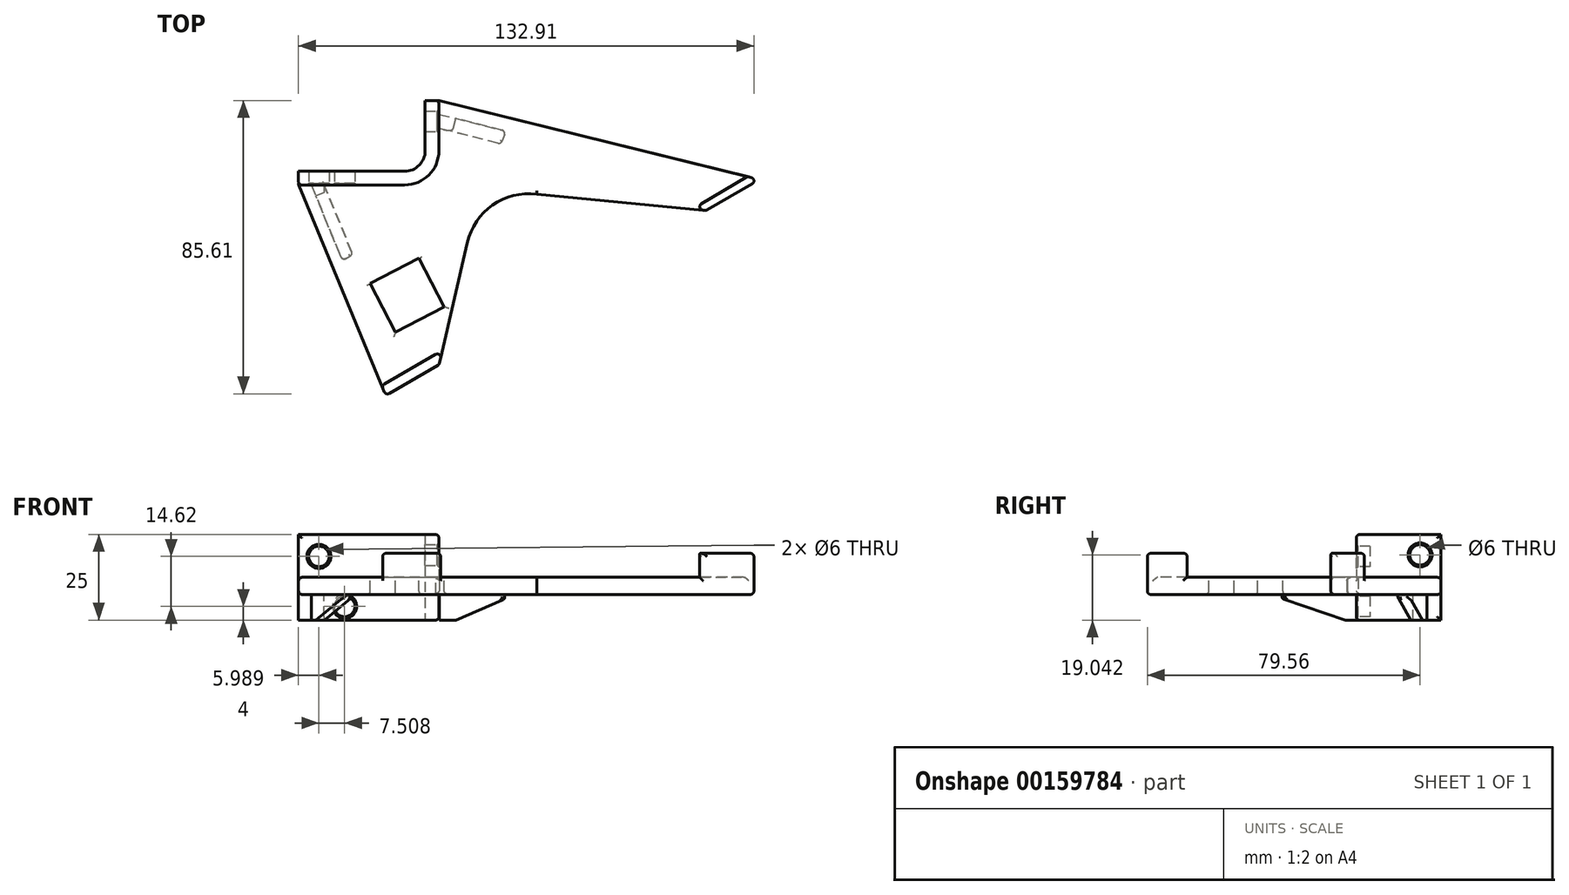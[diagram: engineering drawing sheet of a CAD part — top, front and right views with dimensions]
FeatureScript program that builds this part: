
annotation { "Feature Type Name" : "Feature", "Feature Type Description" : "" }
export const myFeature = defineFeature(function(context is Context, id is Id, definition is map)
    precondition{}
    {
        {
            var Q0;
            Q0=qCreatedBy(makeId("Top.planeOp"),FACE);
            var sketch = newSketch(context, id + "F0", { "sketchPlane" : qUnion([Q0])});
            skLineSegment(sketch, "E0", {"start": v(0, 24.64) * mm, "end": v(0, 10) * mm});
            skLineSegment(sketch, "E1", {"start": v(-41, 0) * mm, "end": v(-10, 0) * mm});
            skPoint(sketch, "E2.visualSharp", {"position": v(0, 0) * mm});
            skArc(sketch, "E2.filletArc", {"start": v(-10, 0) * mm, "mid": v(-2.93, 2.93) * mm, "end": v(0, 10) * mm});
            skLineSegment(sketch, "E3.0", {"start": v(-4, 24.64) * mm, "end": v(-4, 10) * mm});
            skArc(sketch, "E3.1", {"start": v(-10, 4) * mm, "mid": v(-5.76, 5.76) * mm, "end": v(-4, 10) * mm});
            skLineSegment(sketch, "E3.2", {"start": v(-41, 4) * mm, "end": v(-10, 4) * mm});
            skLineSegment(sketch, "E4", {"start": v(-4, 24.64) * mm, "end": v(-4, 24.64) * mm});
            skPoint(sketch, "E5.end.orphan", {"position": v(0, 30.23) * mm});
            skPoint(sketch, "E6.orphan", {"position": v(-2.7, 27.44) * mm});
            skPoint(sketch, "E7.start.orphan", {"position": v(0, 27.44) * mm});
            skLineSegment(sketch, "E8", {"start": v(0, 24.64) * mm, "end": v(-4, 24.64) * mm});
            skLineSegment(sketch, "E9", {"start": v(-41, 4) * mm, "end": v(-41, 0) * mm});
            skLineSegment(sketch, "E10", {"start": v(0, 0) * mm, "end": v(-66, 0) * mm});
            skLineSegment(sketch, "E11", {"start": v(-66, 0) * mm, "end": v(-66, -100) * mm});
            skLineSegment(sketch, "E12", {"start": v(-66, 0) * mm, "end": v(-66, 0) * mm});
            skLineSegment(sketch, "E13", {"start": v(0, 0) * mm, "end": v(-41, 0) * mm});
            skLineSegment(sketch, "E14", {"start": v(-25.5, 0) * mm, "end": v(-41, 0) * mm});
            skLineSegment(sketch, "E15.bottom", {"start": v(-22.01, -78.96) * mm, "end": v(134.2, 11.23) * mm});
            skLineSegment(sketch, "E15.top", {"start": v(0.49, -117.93) * mm, "end": v(156.7, -27.74) * mm});
            skLineSegment(sketch, "E15.left", {"start": v(-22.01, -78.96) * mm, "end": v(0.49, -117.93) * mm});
            skLineSegment(sketch, "E16", {"start": v(0, 24.64) * mm, "end": v(93.48, 1.57) * mm});
            skLineSegment(sketch, "E17", {"start": v(-41, 0) * mm, "end": v(-15.59, -61.4) * mm});
            skLineSegment(sketch, "E18", {"start": v(-15.59, -61.4) * mm, "end": v(0, -52.4) * mm});
            skLineSegment(sketch, "E19", {"start": v(93.48, 1.57) * mm, "end": v(77.9, -7.43) * mm});
            skLineSegment(sketch, "E20", {"start": v(77.9, -7.43) * mm, "end": v(28.44, -2.71) * mm});
            skLineSegment(sketch, "E21", {"start": v(0, -52.4) * mm, "end": v(8.17, -16.87) * mm});
            skArc(sketch, "E22", {"start": v(28.44, -2.71) * mm, "mid": v(15.58, -5.89) * mm, "end": v(8.17, -16.87) * mm});
            skLineSegment(sketch, "E23", {"start": v(13.32, -41.68) * mm, "end": v(-9.18, -2.7) * mm});
            skSolve(sketch);
        }
        {
            var Q0;
            Q0=qSketchRegion(id+"F0",true);
            extrude(context, id + "F1", {"entities" : qUnion([Q0]), "endBound" : BoundingType.SYMMETRIC, "depth" : 5 * mm});
        }
        {
            var Q0;
            Q0=qCreatedBy(makeId("Top.planeOp"),FACE);
            var sketch = newSketch(context, id + "F2", { "sketchPlane" : qUnion([Q0])});
            skLineSegment(sketch, "E24", {"start": v(-0.08, 24.65) * mm, "end": v(-0.08, 10.01) * mm});
            skArc(sketch, "E25.filletArc", {"start": v(-10.08, 0.01) * mm, "mid": v(-3, 2.94) * mm, "end": v(-0.08, 10.01) * mm});
            skLineSegment(sketch, "E26.0", {"start": v(-4.08, 24.65) * mm, "end": v(-4.08, 10.01) * mm});
            skArc(sketch, "E26.1", {"start": v(-10.08, 4.01) * mm, "mid": v(-5.84, 5.77) * mm, "end": v(-4.08, 10.01) * mm});
            skLineSegment(sketch, "E26.2", {"start": v(-41.08, 4.01) * mm, "end": v(-10.08, 4.01) * mm});
            skLineSegment(sketch, "E27", {"start": v(-9.33, 43.65) * mm, "end": v(-9.33, 43.65) * mm});
            skLineSegment(sketch, "E28", {"start": v(-0.08, 24.65) * mm, "end": v(-4.08, 24.65) * mm});
            skLineSegment(sketch, "E29", {"start": v(-41.08, 4.01) * mm, "end": v(-41.08, 0.01) * mm});
            skLineSegment(sketch, "E30", {"start": v(-10.08, 0.01) * mm, "end": v(-41.08, 0.01) * mm});
            skSolve(sketch);
        }
        {
            var Q0;
            Q0=qSketchRegion(id+"F2",true);
            extrude(context, id + "F3", {"entities" : qUnion([Q0]), "operationType" : NewBodyOperationType.ADD, "depth" : 15 * mm, "hasSecondDirection" : true, "secondDirectionOppositeDirection" : true, "secondDirectionDepth" : 10 * mm});
        }
        {
            var Q0;
            Q0=qCreatedBy(makeId("Top.planeOp"),FACE);
            var sketch = newSketch(context, id + "F4", { "sketchPlane" : qUnion([Q0])});
            skLineSegment(sketch, "E31", {"start": v(-40.71, 0) * mm, "end": v(-31.48, -22.47) * mm});
            skLineSegment(sketch, "E32", {"start": v(-37.87, 1.4) * mm, "end": v(-28.24, -22.05) * mm});
            skLineSegment(sketch, "E33", {"start": v(-28.24, -22.05) * mm, "end": v(-25.23, -20.31) * mm});
            skLineSegment(sketch, "E34", {"start": v(-25.23, -20.31) * mm, "end": v(-34.15, 1.4) * mm});
            skLineSegment(sketch, "E35", {"start": v(-34.15, 1.4) * mm, "end": v(-37.87, 1.4) * mm});
            skSolve(sketch);
        }
        {
            var Q0;
            Q0 = qSketchRegion(id + "F4", true);
            extrude(context, id + "F5", {"entities" : qUnion([Q0]), "operationType" : NewBodyOperationType.ADD, "oppositeDirection" : true, "depth" : 10 * mm});
        }
        {
            var Q0;
            Q0=qCreatedBy(makeId("Top.planeOp"),FACE);
            var sketch = newSketch(context, id + "F6", { "sketchPlane" : qUnion([Q0])});
            skLineSegment(sketch, "E36", {"start": v(-41.47, 0) * mm, "end": v(-37.36, 0) * mm});
            skLineSegment(sketch, "E37", {"start": v(0, 20.6) * mm, "end": v(19.4, 15.74) * mm});
            skLineSegment(sketch, "E38", {"start": v(19.4, 15.74) * mm, "end": v(18.07, 11.97) * mm});
            skLineSegment(sketch, "E39", {"start": v(18.07, 11.97) * mm, "end": v(0, 16.49) * mm});
            skLineSegment(sketch, "E40", {"start": v(0, 16.49) * mm, "end": v(0, 20.6) * mm});
            skLineSegment(sketch, "E41", {"start": v(0, 18.54) * mm, "end": v(0, 20.6) * mm});
            skSolve(sketch);
        }
        {
            var Q0;
            Q0 = qSketchRegion(id + "F6", true);
            extrude(context, id + "F7", {"entities" : qUnion([Q0]), "operationType" : NewBodyOperationType.ADD, "oppositeDirection" : true, "depth" : 10 * mm});
        }
        {
            var Q0;
            Q0=qCreatedBy(makeId("Top.planeOp"),FACE);
            var sketch = newSketch(context, id + "F8", { "sketchPlane" : qUnion([Q0])});
            skLineSegment(sketch, "E42.bottom", {"start": v(-20.1, -28.78) * mm, "end": v(-5.9, -21.4) * mm});
            skLineSegment(sketch, "E42.top", {"start": v(-12.73, -42.97) * mm, "end": v(1.47, -35.6) * mm});
            skLineSegment(sketch, "E42.left", {"start": v(-20.1, -28.78) * mm, "end": v(-12.73, -42.97) * mm});
            skLineSegment(sketch, "E42.right", {"start": v(-5.9, -21.4) * mm, "end": v(1.47, -35.6) * mm});
            skSolve(sketch);
        }
        {
            var Q0;
            Q0 = qSketchRegion(id + "F8", true);
            extrude(context, id + "F9", {"entities" : qUnion([Q0]), "operationType" : NewBodyOperationType.REMOVE, "endBound" : BoundingType.SYMMETRIC, "oppositeDirection" : true, "depth" : 25 * mm});
        }
        {
            var Q0;
            Q0=makeQuery(id+"F5.opExtrude","SWEPT_FACE",FACE,{"disambiguationData":[OSD([sQuery(id+"F4.wireOp",EDGE,"E32")])]});
            var sketch = newSketch(context, id + "F10", { "sketchPlane" : qUnion([Q0])});
            skLineSegment(sketch, "E43", {"start": v(9.66, -3.57) * mm, "end": v(-10.72, -10) * mm});
            skLineSegment(sketch, "E44", {"start": v(-10.72, -10) * mm, "end": v(9.66, -10) * mm});
            skLineSegment(sketch, "E45", {"start": v(9.66, -10) * mm, "end": v(9.66, -3.57) * mm});
            skSolve(sketch);
        }
        {
            var Q0;
            Q0=makeQuery(id+"F10.imprint","IMPRINT",FACE,{"disambiguationData":[TD([[makeQuery(id+"F10.imprint","IMPRINT",EDGE,{"derivedFrom":sQuery(id+"F10.wireOp",EDGE,"E43")}),1.0]])]});
            extrude(context, id + "F11", {"entities" : qUnion([Q0]), "operationType" : NewBodyOperationType.REMOVE, "oppositeDirection" : true, "depth" : 7 * mm});
        }
        {
            var Q0;
            Q0=makeQuery(id+"F7.opExtrude","SWEPT_FACE",FACE,{"disambiguationData":[OSD([sQuery(id+"F6.wireOp",EDGE,"E37")])]});
            var sketch = newSketch(context, id + "F12", { "sketchPlane" : qUnion([Q0])});
            skLineSegment(sketch, "E46", {"start": v(-15, -3.7) * mm, "end": v(0, -10) * mm});
            skLineSegment(sketch, "E47", {"start": v(0, -10) * mm, "end": v(-15, -10) * mm});
            skLineSegment(sketch, "E48", {"start": v(-15, -10) * mm, "end": v(-15, -3.7) * mm});
            skSolve(sketch);
        }
        {
            var Q0;
            Q0=makeQuery(id+"F12.imprint","IMPRINT",FACE,{"disambiguationData":[TD([[makeQuery(id+"F12.imprint","IMPRINT",EDGE,{"derivedFrom":sQuery(id+"F12.wireOp",EDGE,"E46")}),-1.0]])]});
            extrude(context, id + "F13", {"entities" : qUnion([Q0]), "operationType" : NewBodyOperationType.REMOVE, "oppositeDirection" : true, "depth" : 7 * mm});
        }
        {
            var Q0;
            Q0=makeQuery(id+"F1.opExtrude","CAP_FACE",FACE,{"disambiguationData":[OSD([sQuery(id+"F0.wireOp",EDGE,"E3.0"),sQuery(id+"F0.wireOp",EDGE,"E3.1"),sQuery(id+"F0.wireOp",EDGE,"E3.2"),sQuery(id+"F0.wireOp",EDGE,"E8"),sQuery(id+"F0.wireOp",EDGE,"E9"),sQuery(id+"F0.wireOp",EDGE,"E16"),sQuery(id+"F0.wireOp",EDGE,"E17"),sQuery(id+"F0.wireOp",EDGE,"E18"),sQuery(id+"F0.wireOp",EDGE,"E19"),sQuery(id+"F0.wireOp",EDGE,"E20"),sQuery(id+"F0.wireOp",EDGE,"E21"),sQuery(id+"F0.wireOp",EDGE,"E22")])],"isStart":false});
            var sketch = newSketch(context, id + "F14", { "sketchPlane" : qUnion([Q0])});
            skLineSegment(sketch, "E49", {"start": v(-15.59, -61.4) * mm, "end": v(0, -52.4) * mm});
            skLineSegment(sketch, "E50", {"start": v(0, -52.4) * mm, "end": v(0.94, -48.3) * mm});
            skLineSegment(sketch, "E51", {"start": v(0.94, -48.3) * mm, "end": v(-16.77, -58.54) * mm});
            skLineSegment(sketch, "E52", {"start": v(-16.77, -58.54) * mm, "end": v(-15.59, -61.4) * mm});
            skSolve(sketch);
        }
        {
            var Q0;
            Q0=makeQuery(id+"F14.imprint","IMPRINT",FACE,{"disambiguationData":[TD([[makeQuery(id+"F14.imprint","IMPRINT",EDGE,{"derivedFrom":sQuery(id+"F14.wireOp",EDGE,"E49")}),1.0]])]});
            extrude(context, id + "F15", {"entities" : qUnion([Q0]), "operationType" : NewBodyOperationType.ADD, "depth" : 7 * mm});
        }
        {
            var Q0;
            Q0=makeQuery(id+"F1.opExtrude","CAP_FACE",FACE,{"disambiguationData":[OSD([sQuery(id+"F0.wireOp",EDGE,"E3.0"),sQuery(id+"F0.wireOp",EDGE,"E3.1"),sQuery(id+"F0.wireOp",EDGE,"E3.2"),sQuery(id+"F0.wireOp",EDGE,"E8"),sQuery(id+"F0.wireOp",EDGE,"E9"),sQuery(id+"F0.wireOp",EDGE,"E16"),sQuery(id+"F0.wireOp",EDGE,"E17"),sQuery(id+"F0.wireOp",EDGE,"E18"),sQuery(id+"F0.wireOp",EDGE,"E19"),sQuery(id+"F0.wireOp",EDGE,"E20"),sQuery(id+"F0.wireOp",EDGE,"E21"),sQuery(id+"F0.wireOp",EDGE,"E22")])],"isStart":false});
            var sketch = newSketch(context, id + "F16", { "sketchPlane" : qUnion([Q0])});
            skLineSegment(sketch, "E53", {"start": v(77.9, -7.43) * mm, "end": v(93.48, 1.57) * mm});
            skLineSegment(sketch, "E54", {"start": v(93.48, 1.57) * mm, "end": v(89.9, 2.46) * mm});
            skLineSegment(sketch, "E55", {"start": v(89.9, 2.46) * mm, "end": v(73.9, -7.05) * mm});
            skLineSegment(sketch, "E56", {"start": v(73.9, -7.05) * mm, "end": v(77.9, -7.43) * mm});
            skSolve(sketch);
        }
        {
            var Q0;
            Q0=makeQuery(id+"F16.imprint","IMPRINT",FACE,{"disambiguationData":[TD([[makeQuery(id+"F16.imprint","IMPRINT",EDGE,{"derivedFrom":sQuery(id+"F16.wireOp",EDGE,"E53")}),-1.0]])]});
            extrude(context, id + "F17", {"entities" : qUnion([Q0]), "operationType" : NewBodyOperationType.ADD, "depth" : 7 * mm});
        }
        {
            var Q0;
            Q0=makeQuery(id+"FxJEatKh2n8C777_1.opFillet","SPLIT",FACE,{"disambiguationData":[OD(1.0)],"derivedFrom":makeQuery(id+"F3.opExtrude","SWEPT_FACE",FACE,{"disambiguationData":[OSD([sQuery(id+"F2.wireOp",EDGE,"E30")])]})});
            var sketch = newSketch(context, id + "F18", { "sketchPlane" : qUnion([Q0])});
            skLineSegment(sketch, "E57.bottom", {"start": v(-41.1, 14.62) * mm, "end": v(-35.1, 14.62) * mm});
            skLineSegment(sketch, "E57.top", {"start": v(-41.1, 8.62) * mm, "end": v(-35.1, 8.62) * mm});
            skLineSegment(sketch, "E57.left", {"start": v(-41.1, 14.62) * mm, "end": v(-41.1, 8.62) * mm});
            skLineSegment(sketch, "E57.right", {"start": v(-35.1, 14.62) * mm, "end": v(-35.1, 8.62) * mm});
            skPoint(sketch, "E58", {"position": v(-35.1, 8.62) * mm});
            skSolve(sketch);
        }
        {
            var Q0;
            {var subQ1=sQuery(id+"F4.wireOp",EDGE,"E34");var subQ2=sQuery(id+"F2.wireOp",EDGE,"E30");Q0=makeQuery(id+"F5.boolean.opBoolean","SPLIT",FACE,{"disambiguationData":[TD([makeQuery(id+"F5.opExtrude","SWEPT_FACE",FACE,{"disambiguationData":[OSD([subQ1])]})])],"derivedFrom":makeQuery(id+"F3.opExtrude","SWEPT_FACE",FACE,{"disambiguationData":[OSD([subQ2])]})});}
            var sketch = newSketch(context, id + "F19", { "sketchPlane" : qUnion([Q0])});
            skLineSegment(sketch, "E59.bottom", {"start": v(-33.58, -10) * mm, "end": v(-27.58, -10) * mm});
            skLineSegment(sketch, "E59.top", {"start": v(-33.58, -6) * mm, "end": v(-27.58, -6) * mm});
            skLineSegment(sketch, "E59.left", {"start": v(-33.58, -10) * mm, "end": v(-33.58, -6) * mm});
            skLineSegment(sketch, "E59.right", {"start": v(-27.58, -10) * mm, "end": v(-27.58, -6) * mm});
            skPoint(sketch, "E60", {"position": v(-27.58, -6) * mm});
            skSolve(sketch);
        }
        {
            var Q0;
            Q0=makeQuery(id+"F3.opExtrude","SWEPT_FACE",FACE,{"disambiguationData":[OSD([sQuery(id+"F2.wireOp",EDGE,"E24")])]});
            var sketch = newSketch(context, id + "F20", { "sketchPlane" : qUnion([Q0])});
            skLineSegment(sketch, "E61.bottom", {"start": v(24.6, 15.04) * mm, "end": v(18.6, 15.04) * mm});
            skLineSegment(sketch, "E61.top", {"start": v(24.6, 9.04) * mm, "end": v(18.6, 9.04) * mm});
            skLineSegment(sketch, "E61.left", {"start": v(24.6, 15.04) * mm, "end": v(24.6, 9.04) * mm});
            skLineSegment(sketch, "E61.right", {"start": v(18.6, 15.04) * mm, "end": v(18.6, 9.04) * mm});
            skPoint(sketch, "E62", {"position": v(18.6, 9.04) * mm});
            skSolve(sketch);
        }
        {
            var Q0;
            Q0=sQuery(id+"F18.wireOp",VERTEX,"E58");
            var Q1;
            Q1=sQuery(id+"F20.wireOp",VERTEX,"E62");
            var Q2;
            Q2=sQuery(id+"F19.wireOp",VERTEX,"E60");
            var Q3;
            Q3=makeQuery(id+"F1.opExtrude","SWEPT_BODY",BODY,{"disambiguationData":[OSD([sQuery(id+"F0.wireOp",EDGE,"E3.0"),sQuery(id+"F0.wireOp",EDGE,"E3.1"),sQuery(id+"F0.wireOp",EDGE,"E3.2"),sQuery(id+"F0.wireOp",EDGE,"E8"),sQuery(id+"F0.wireOp",EDGE,"E9"),sQuery(id+"F0.wireOp",EDGE,"E16"),sQuery(id+"F0.wireOp",EDGE,"E17"),sQuery(id+"F0.wireOp",EDGE,"E18"),sQuery(id+"F0.wireOp",EDGE,"E19"),sQuery(id+"F0.wireOp",EDGE,"E20"),sQuery(id+"F0.wireOp",EDGE,"E21"),sQuery(id+"F0.wireOp",EDGE,"E22")])]});
            hole(context, id + "F21", {"style" : HoleStyle.C_SINK, "endStyle" : HoleEndStyle.THROUGH, "holeDiameter" : 6 * mm, "cSinkDiameter" : 7 * mm, "cSinkAngle" : 90 * degree, "locations" : qUnion([Q0, Q1, Q2]), "scope" : qUnion([Q3]), "isTappedThrough" : true});
        }
        {
            var Q0;
            Q0=makeQuery(id+"F15.boolean.opBoolean","MERGE",EDGE,{"derivedFrom":[makeQuery(id+"F1.opExtrude","SWEPT_EDGE",EDGE,{"disambiguationData":[OSD([sQuery(id+"F0.wireOp",EDGE,"E17"),sQuery(id+"F0.wireOp",EDGE,"E18")])]}),makeQuery(id+"F15.opExtrude","SWEPT_EDGE",EDGE,{"disambiguationData":[OSD([sQuery(id+"F14.wireOp",EDGE,"E49"),sQuery(id+"F14.wireOp",EDGE,"E52")])]})]});
            var Q1;
            Q1=makeQuery(id+"F15.boolean.opBoolean","MERGE",FACE,{"derivedFrom":[makeQuery(id+"F1.opExtrude","SWEPT_FACE",FACE,{"disambiguationData":[OSD([sQuery(id+"F0.wireOp",EDGE,"E18")])]}),makeQuery(id+"F15.opExtrude","SWEPT_FACE",FACE,{"disambiguationData":[OSD([sQuery(id+"F14.wireOp",EDGE,"E49")])]})]});
            var Q2;
            Q2=makeQuery(id+"F1.opExtrude","CAP_EDGE",EDGE,{"disambiguationData":[OSD([sQuery(id+"F0.wireOp",EDGE,"E17")])],"isStart":false});
            var Q3;
            Q3=makeQuery(id+"F15.boolean.opBoolean","MERGE",FACE,{"derivedFrom":[makeQuery(id+"F1.opExtrude","SWEPT_FACE",FACE,{"disambiguationData":[OSD([sQuery(id+"F0.wireOp",EDGE,"E17")])]}),makeQuery(id+"F15.opExtrude","SWEPT_FACE",FACE,{"disambiguationData":[OSD([sQuery(id+"F14.wireOp",EDGE,"E52")])]})]});
            var Q4;
            Q4=makeQuery(id+"F15.boolean.opBoolean","MERGE",FACE,{"derivedFrom":[makeQuery(id+"F1.opExtrude","SWEPT_FACE",FACE,{"disambiguationData":[OSD([sQuery(id+"F0.wireOp",EDGE,"E21")])]}),makeQuery(id+"F15.opExtrude","SWEPT_FACE",FACE,{"disambiguationData":[OSD([sQuery(id+"F14.wireOp",EDGE,"E50")])]})]});
            var Q5;
            Q5=makeQuery(id+"F1.opExtrude","CAP_EDGE",EDGE,{"disambiguationData":[OSD([sQuery(id+"F0.wireOp",EDGE,"E20")])],"isStart":false});
            var Q6;
            Q6=makeQuery(id+"F1.opExtrude","CAP_EDGE",EDGE,{"disambiguationData":[OSD([sQuery(id+"F0.wireOp",EDGE,"E20")])],"isStart":true});
            var Q7;
            Q7=makeQuery(id+"F11.boolean.opBoolean","INTERSECT",EDGE,{"derivedFrom":[makeQuery(id+"F5.opExtrude","SWEPT_FACE",FACE,{"disambiguationData":[OSD([sQuery(id+"F4.wireOp",EDGE,"E33")])]}),makeQuery(id+"F11.opExtrude","SWEPT_FACE",FACE,{"disambiguationData":[OSD([sQuery(id+"F10.wireOp",EDGE,"E43")])]})]});
            var Q8;
            Q8=makeQuery(id+"F11.boolean.opBoolean","COPY",EDGE,{"derivedFrom":makeQuery(id+"F11.opExtrude","CAP_EDGE",EDGE,{"disambiguationData":[OSD([sQuery(id+"F10.wireOp",EDGE,"E43")])],"isStart":true})});
            var Q9;
            Q9=makeQuery(id+"F5.opExtrude","SWEPT_EDGE",EDGE,{"disambiguationData":[OSD([sQuery(id+"F4.wireOp",EDGE,"E33"),sQuery(id+"F4.wireOp",EDGE,"E34")])]});
            var Q10;
            Q10=makeQuery(id+"F11.boolean.opBoolean","INTERSECT",EDGE,{"derivedFrom":[makeQuery(id+"F5.opExtrude","SWEPT_FACE",FACE,{"disambiguationData":[OSD([sQuery(id+"F4.wireOp",EDGE,"E34")])]}),makeQuery(id+"F11.opExtrude","SWEPT_FACE",FACE,{"disambiguationData":[OSD([sQuery(id+"F10.wireOp",EDGE,"E43")])]})]});
            var Q11;
            Q11=makeQuery(id+"F5.opExtrude","SWEPT_EDGE",EDGE,{"disambiguationData":[OSD([sQuery(id+"F4.wireOp",EDGE,"E32"),sQuery(id+"F4.wireOp",EDGE,"E33")])]});
            var Q12;
            Q12=makeQuery(id+"F13.boolean.opBoolean","INTERSECT",EDGE,{"derivedFrom":[makeQuery(id+"F7.opExtrude","SWEPT_FACE",FACE,{"disambiguationData":[OSD([sQuery(id+"F6.wireOp",EDGE,"E39")])]}),makeQuery(id+"F13.opExtrude","SWEPT_FACE",FACE,{"disambiguationData":[OSD([sQuery(id+"F12.wireOp",EDGE,"E46")])]})]});
            var Q13;
            Q13=makeQuery(id+"F7.opExtrude","SWEPT_EDGE",EDGE,{"disambiguationData":[OSD([sQuery(id+"F6.wireOp",EDGE,"E38"),sQuery(id+"F6.wireOp",EDGE,"E39")])]});
            var Q14;
            Q14=makeQuery(id+"F7.opExtrude","SWEPT_EDGE",EDGE,{"disambiguationData":[OSD([sQuery(id+"F6.wireOp",EDGE,"E37"),sQuery(id+"F6.wireOp",EDGE,"E38")])]});
            var Q15;
            Q15=makeQuery(id+"F1.opExtrude","CAP_EDGE",EDGE,{"disambiguationData":[OSD([sQuery(id+"F0.wireOp",EDGE,"E16")])],"isStart":false});
            var Q16;
            Q16=makeQuery(id+"F17.opExtrude","SWEPT_EDGE",EDGE,{"disambiguationData":[OSD([sQuery(id+"F0.wireOp",EDGE,"E16"),sQuery(id+"F16.wireOp",EDGE,"E54"),sQuery(id+"F16.wireOp",EDGE,"E55")])]});
            var Q17;
            Q17=makeQuery(id+"F13.boolean.opBoolean","INTERSECT",EDGE,{"derivedFrom":[makeQuery(id+"F7.opExtrude","SWEPT_FACE",FACE,{"disambiguationData":[OSD([sQuery(id+"F6.wireOp",EDGE,"E38")])]}),makeQuery(id+"F13.opExtrude","SWEPT_FACE",FACE,{"disambiguationData":[OSD([sQuery(id+"F12.wireOp",EDGE,"E46")])]})]});
            var Q18;
            Q18=makeQuery(id+"F13.boolean.opBoolean","COPY",EDGE,{"derivedFrom":makeQuery(id+"F13.opExtrude","CAP_EDGE",EDGE,{"disambiguationData":[OSD([sQuery(id+"F12.wireOp",EDGE,"E46")])],"isStart":true})});
            var Q19;
            Q19=makeQuery(id+"F9.boolean.opBoolean","INTERSECT",EDGE,{"derivedFrom":[makeQuery(id+"F1.opExtrude","CAP_FACE",FACE,{"disambiguationData":[OSD([sQuery(id+"F0.wireOp",EDGE,"E3.0"),sQuery(id+"F0.wireOp",EDGE,"E3.1"),sQuery(id+"F0.wireOp",EDGE,"E3.2"),sQuery(id+"F0.wireOp",EDGE,"E8"),sQuery(id+"F0.wireOp",EDGE,"E9"),sQuery(id+"F0.wireOp",EDGE,"E16"),sQuery(id+"F0.wireOp",EDGE,"E17"),sQuery(id+"F0.wireOp",EDGE,"E18"),sQuery(id+"F0.wireOp",EDGE,"E19"),sQuery(id+"F0.wireOp",EDGE,"E20"),sQuery(id+"F0.wireOp",EDGE,"E21"),sQuery(id+"F0.wireOp",EDGE,"E22")])],"isStart":true}),makeQuery(id+"F9.opExtrude","SWEPT_FACE",FACE,{"disambiguationData":[OSD([sQuery(id+"F8.wireOp",EDGE,"E42.left")])]})]});
            var Q20;
            Q20=makeQuery(id+"F9.boolean.opBoolean","INTERSECT",EDGE,{"derivedFrom":[makeQuery(id+"F1.opExtrude","CAP_FACE",FACE,{"disambiguationData":[OSD([sQuery(id+"F0.wireOp",EDGE,"E3.0"),sQuery(id+"F0.wireOp",EDGE,"E3.1"),sQuery(id+"F0.wireOp",EDGE,"E3.2"),sQuery(id+"F0.wireOp",EDGE,"E8"),sQuery(id+"F0.wireOp",EDGE,"E9"),sQuery(id+"F0.wireOp",EDGE,"E16"),sQuery(id+"F0.wireOp",EDGE,"E17"),sQuery(id+"F0.wireOp",EDGE,"E18"),sQuery(id+"F0.wireOp",EDGE,"E19"),sQuery(id+"F0.wireOp",EDGE,"E20"),sQuery(id+"F0.wireOp",EDGE,"E21"),sQuery(id+"F0.wireOp",EDGE,"E22")])],"isStart":true}),makeQuery(id+"F9.opExtrude","SWEPT_FACE",FACE,{"disambiguationData":[OSD([sQuery(id+"F8.wireOp",EDGE,"E42.right")])]})]});
            var Q21;
            Q21=makeQuery(id+"F9.boolean.opBoolean","INTERSECT",EDGE,{"derivedFrom":[makeQuery(id+"F1.opExtrude","CAP_FACE",FACE,{"disambiguationData":[OSD([sQuery(id+"F0.wireOp",EDGE,"E3.0"),sQuery(id+"F0.wireOp",EDGE,"E3.1"),sQuery(id+"F0.wireOp",EDGE,"E3.2"),sQuery(id+"F0.wireOp",EDGE,"E8"),sQuery(id+"F0.wireOp",EDGE,"E9"),sQuery(id+"F0.wireOp",EDGE,"E16"),sQuery(id+"F0.wireOp",EDGE,"E17"),sQuery(id+"F0.wireOp",EDGE,"E18"),sQuery(id+"F0.wireOp",EDGE,"E19"),sQuery(id+"F0.wireOp",EDGE,"E20"),sQuery(id+"F0.wireOp",EDGE,"E21"),sQuery(id+"F0.wireOp",EDGE,"E22")])],"isStart":true}),makeQuery(id+"F9.opExtrude","SWEPT_FACE",FACE,{"disambiguationData":[OSD([sQuery(id+"F8.wireOp",EDGE,"E42.top")])]})]});
            var Q22;
            Q22=makeQuery(id+"F17.boolean.opBoolean","MERGE",EDGE,{"derivedFrom":[makeQuery(id+"F1.opExtrude","SWEPT_EDGE",EDGE,{"disambiguationData":[OSD([sQuery(id+"F0.wireOp",EDGE,"E16"),sQuery(id+"F0.wireOp",EDGE,"E19")])]}),makeQuery(id+"F17.opExtrude","SWEPT_EDGE",EDGE,{"disambiguationData":[OSD([sQuery(id+"F16.wireOp",EDGE,"E53"),sQuery(id+"F16.wireOp",EDGE,"E54")])]})]});
            var Q23;
            Q23=makeQuery(id+"F1.opExtrude","CAP_EDGE",EDGE,{"disambiguationData":[OSD([sQuery(id+"F0.wireOp",EDGE,"E16")])],"isStart":true});
            var Q24;
            Q24=makeQuery(id+"F17.opExtrude","CAP_EDGE",EDGE,{"disambiguationData":[OSD([sQuery(id+"F16.wireOp",EDGE,"E53")])],"isStart":false});
            var Q25;
            Q25=makeQuery(id+"F17.boolean.opBoolean","MERGE",EDGE,{"derivedFrom":[makeQuery(id+"F1.opExtrude","SWEPT_EDGE",EDGE,{"disambiguationData":[OSD([sQuery(id+"F0.wireOp",EDGE,"E19"),sQuery(id+"F0.wireOp",EDGE,"E20")])]}),makeQuery(id+"F17.opExtrude","SWEPT_EDGE",EDGE,{"disambiguationData":[OSD([sQuery(id+"F16.wireOp",EDGE,"E53"),sQuery(id+"F16.wireOp",EDGE,"E56")])]})]});
            fillet(context, id + "F22", {"entities" : qUnion([Q0, Q1, Q2, Q3, Q4, Q5, Q6, Q7, Q8, Q9, Q10, Q11, Q12, Q13, Q14, Q15, Q16, Q17, Q18, Q19, Q20, Q21, Q22, Q23, Q24, Q25]), "radius" : 1 * mm, "tangentPropagation" : true, "allowEdgeOverflow" : false});
        }
        {
            var Q0;
            Q0=makeQuery(id+"F22.opFillet","BLEND_FACE",FACE,{"disambiguationData":[OSD([sQuery(id+"F0.wireOp",EDGE,"E16"),sQuery(id+"F0.wireOp",EDGE,"E19"),sQuery(id+"F16.wireOp",EDGE,"E53"),sQuery(id+"F16.wireOp",EDGE,"E54")])]});
            var Q1;
            Q1=makeQuery(id+"F3.opExtrude","CAP_EDGE",EDGE,{"disambiguationData":[OSD([sQuery(id+"F2.wireOp",EDGE,"E24")])],"isStart":false});
            var Q2;
            Q2=makeQuery(id+"F3.opExtrude","SWEPT_EDGE",EDGE,{"disambiguationData":[OSD([sQuery(id+"F2.wireOp",EDGE,"E24"),sQuery(id+"F2.wireOp",EDGE,"E28")])]});
            var Q3;
            Q3=makeQuery(id+"F3.opExtrude","CAP_EDGE",EDGE,{"disambiguationData":[OSD([sQuery(id+"F2.wireOp",EDGE,"E24")])],"isStart":true});
            var Q4;
            Q4=makeQuery(id+"F17.opExtrude","SWEPT_EDGE",EDGE,{"disambiguationData":[OSD([sQuery(id+"F0.wireOp",EDGE,"E20"),sQuery(id+"F16.wireOp",EDGE,"E55"),sQuery(id+"F16.wireOp",EDGE,"E56")])]});
            var Q5;
            Q5=makeQuery(id+"F3.opExtrude","SWEPT_EDGE",EDGE,{"disambiguationData":[OSD([sQuery(id+"F2.wireOp",EDGE,"E29"),sQuery(id+"F2.wireOp",EDGE,"E30")])]});
            var Q6;
            Q6=makeQuery(id+"F17.opExtrude","CAP_EDGE",EDGE,{"disambiguationData":[OSD([sQuery(id+"F16.wireOp",EDGE,"E55")])],"isStart":false});
            var Q7;
            Q7=makeQuery(id+"F15.opExtrude","CAP_EDGE",EDGE,{"disambiguationData":[OSD([sQuery(id+"F14.wireOp",EDGE,"E51")])],"isStart":false});
            fillet(context, id + "F23", {"entities" : qUnion([Q0, Q1, Q2, Q3, Q4, Q5, Q6, Q7]), "radius" : 1 * mm, "tangentPropagation" : true, "allowEdgeOverflow" : false});
        }
    });
